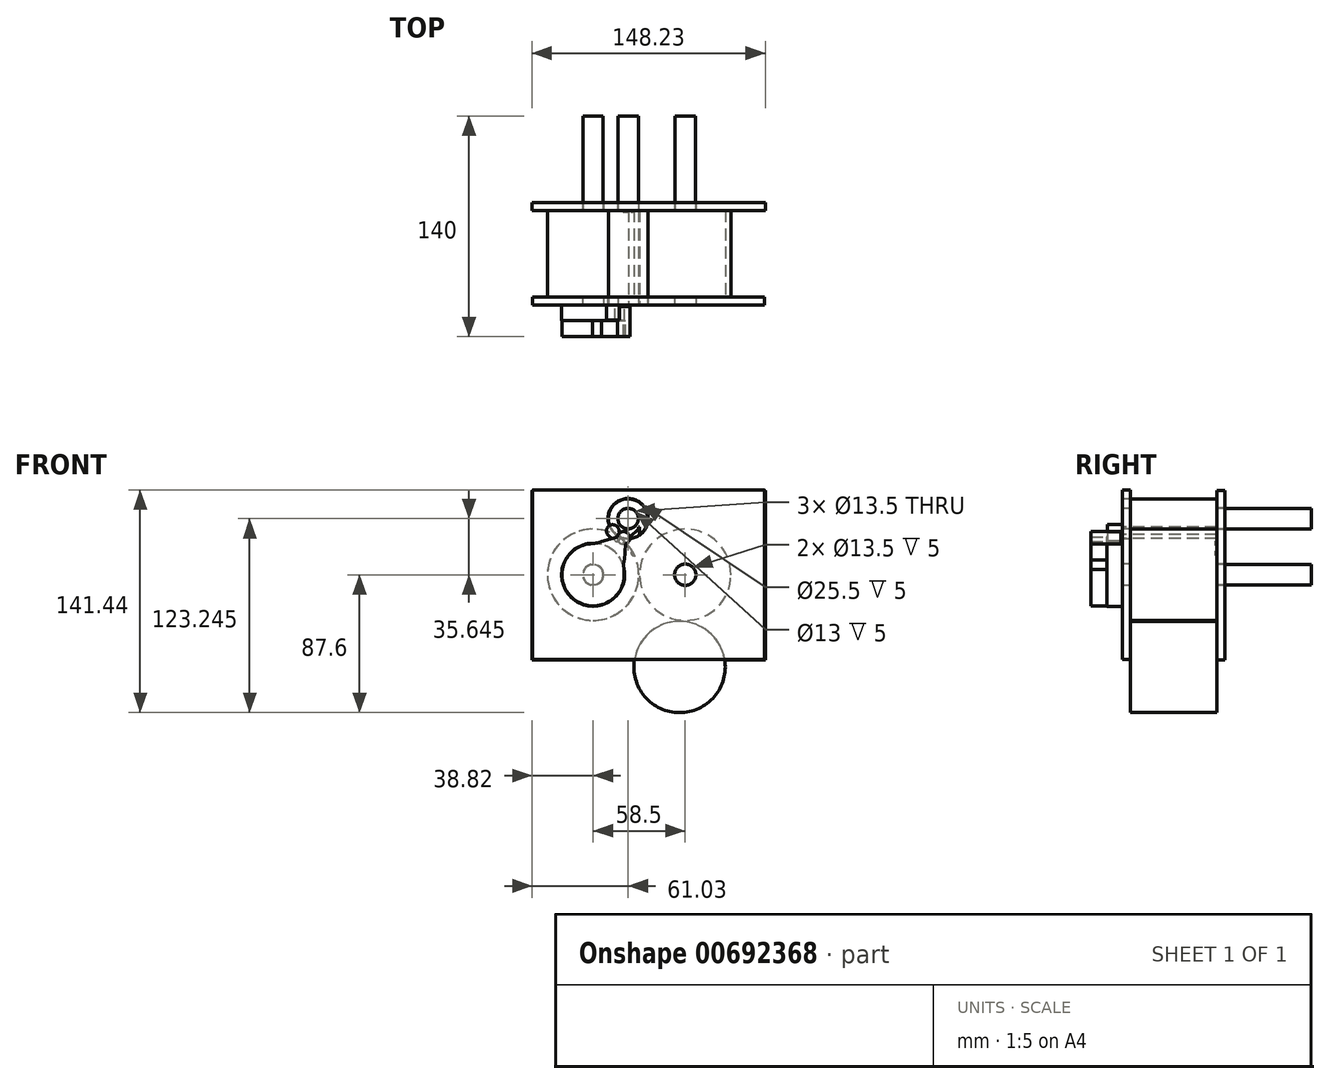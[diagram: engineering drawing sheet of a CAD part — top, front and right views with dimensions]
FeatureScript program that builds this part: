
annotation { "Feature Type Name" : "Feature", "Feature Type Description" : "" }
export const myFeature = defineFeature(function(context is Context, id is Id, definition is map)
    precondition{}
    {
        {
            var Q0;
            Q0=qCreatedBy(makeId("Front.planeOp"),FACE);
            var sketch = newSketch(context, id + "F0", { "sketchPlane" : qUnion([Q0])});
            skArc(sketch, "E0", {"start": v(-42.9, 24.45) * mm, "mid": v(-74.98, -23.86) * mm, "end": v(-41.15, 23.24) * mm});
            skArc(sketch, "E1", {"start": v(-29, 0) * mm, "mid": v(28.64, -4.55) * mm, "end": v(-27.57, 8.99) * mm});
            skCircle(sketch, "E2", {"center": v(-18.44, -37.73) * mm, "radius": 12.5 * mm});
            skCircle(sketch, "E3", {"center": v(-3.57, -58.6) * mm, "radius": 29 * mm});
            skPoint(sketch, "E4.end.orphan", {"position": v(-29.02, 40.63) * mm});
            skPoint(sketch, "E5.orphan", {"position": v(-29.02, 38.55) * mm});
            skPoint(sketch, "E6.orphan", {"position": v(-29.02, 31.65) * mm});
            skPoint(sketch, "E7.start.orphan", {"position": v(-40.21, 34.8) * mm});
            skPoint(sketch, "E8.start.orphan", {"position": v(-29.02, 34.8) * mm});
            skPoint(sketch, "E9.start.orphan", {"position": v(-29.02, 28.5) * mm});
            skLineSegment(sketch, "E10", {"start": v(-28.97, 1.35) * mm, "end": v(-29, 1.35) * mm});
            skPoint(sketch, "E11.orphan", {"position": v(-27.57, 13.81) * mm});
            skPoint(sketch, "E12.endSnap0", {"position": v(-28.5, 2.55) * mm});
            skLineSegment(sketch, "E13", {"start": v(6.21, -31.3) * mm, "end": v(1.47, -32.78) * mm});
            skLineSegment(sketch, "E14", {"start": v(-29.02, 28.5) * mm, "end": v(-29.02, 29) * mm});
            skPoint(sketch, "E15.start.orphan", {"position": v(-48.55, 37.66) * mm});
            skPoint(sketch, "E16.orphan", {"position": v(-57.21, 3.62) * mm});
            skPoint(sketch, "E17.orphan", {"position": v(-63.6, -15.91) * mm});
            skPoint(sketch, "E18.orphan", {"position": v(-48.66, 40.63) * mm});
            skPoint(sketch, "E19.orphan", {"position": v(15.22, 40.63) * mm});
            skPoint(sketch, "E20.start.orphan", {"position": v(13.58, 48.81) * mm});
            skPoint(sketch, "E21.center.orphan", {"position": v(14.4, 44.72) * mm});
            skArc(sketch, "E22.trimOffspring", {"start": v(-63.62, -9.18) * mm, "mid": v(-63.62, -9.18) * mm, "end": v(-63.6, -9.18) * mm});
            skPoint(sketch, "E23.start.orphan", {"position": v(-46.66, 44.1) * mm});
            skPoint(sketch, "E24.center.orphan", {"position": v(-44.88, 44.1) * mm});
            skPoint(sketch, "E25.trimOffspring.start.orphan", {"position": v(-29.02, 29) * mm});
            skPoint(sketch, "E26.orphan", {"position": v(-50.88, 37.66) * mm});
            skPoint(sketch, "E27.end.orphan", {"position": v(-31.73, 29) * mm});
            skPoint(sketch, "E28.orphan", {"position": v(-45.99, 26.74) * mm});
            skPoint(sketch, "E29.center.orphan", {"position": v(-55.66, 3.62) * mm});
            skPoint(sketch, "E30.trimOffspring.end.orphan", {"position": v(-54.97, 9.17) * mm});
            skPoint(sketch, "E31.center.orphan", {"position": v(-53.8, 9.17) * mm});
            skPoint(sketch, "E12.end.orphan", {"position": v(-28.5, 3.54) * mm});
            skPoint(sketch, "E32.start.orphan", {"position": v(-29, 3.74) * mm});
            skPoint(sketch, "E33.center.orphan", {"position": v(-63.6, -1.9) * mm});
            skPoint(sketch, "E34.end.orphan", {"position": v(6.08, 26.74) * mm});
            skLineSegment(sketch, "E35.trimOffspring", {"start": v(-28.98, -31) * mm, "end": v(-28.97, -38.02) * mm});
            skPoint(sketch, "E36.orphan", {"position": v(-28, 1.35) * mm});
            skArc(sketch, "E37", {"start": v(-27.57, 8.99) * mm, "mid": v(-28.64, 4.55) * mm, "end": v(-29, 0) * mm});
            skLineSegment(sketch, "E38", {"start": v(-29, 0) * mm, "end": v(-29.5, 0) * mm});
            skLineSegment(sketch, "E39", {"start": v(-29.25, 0) * mm, "end": v(-29.25, 5) * mm});
            skLineSegment(sketch, "E40", {"start": v(-29.75, 30.46) * mm, "end": v(-29.75, 29.04) * mm});
            skLineSegment(sketch, "E41", {"start": v(-29.05, 25.46) * mm, "end": v(-29.05, 30.46) * mm});
            skLineSegment(sketch, "E42", {"start": v(-29.05, 30.46) * mm, "end": v(-29.75, 30.46) * mm});
            skLineSegment(sketch, "E43", {"start": v(-29.75, 29.04) * mm, "end": v(-36, 23.15) * mm});
            skArc(sketch, "E44.trimOffspring", {"start": v(-29.05, 28.75) * mm, "mid": v(-29.04, 28.76) * mm, "end": v(-29.02, 28.78) * mm});
            skPoint(sketch, "E45.start.orphan", {"position": v(-43.7, 32.57) * mm});
            skPoint(sketch, "E46.orphan", {"position": v(-50.05, 29.86) * mm});
            skPoint(sketch, "E47.center.orphan", {"position": v(-47.7, 29) * mm});
            skLineSegment(sketch, "E48", {"start": v(-36.3, 35.64) * mm, "end": v(-58.26, 0.38) * mm, "construction": true});
            skArc(sketch, "E49", {"start": v(-33, 13.81) * mm, "mid": v(-36.56, 18.98) * mm, "end": v(-41.16, 23.25) * mm});
            skLineSegment(sketch, "E50", {"start": v(-33, 13.81) * mm, "end": v(-54, 2.44) * mm, "construction": true});
            skLineSegment(sketch, "E51", {"start": v(-29.05, 25.46) * mm, "end": v(-36.3, 35.64) * mm, "construction": true});
            skPoint(sketch, "E52.start.orphan", {"position": v(-58.26, -4.58) * mm});
            skLineSegment(sketch, "E53.trimOffspring", {"start": v(-58.26, 0.22) * mm, "end": v(-58.26, 0.38) * mm});
            skLineSegment(sketch, "E54", {"start": v(-54, 2.44) * mm, "end": v(-58.5, 0) * mm, "construction": true});
            skLineSegment(sketch, "E55", {"start": v(-36.3, 35.64) * mm, "end": v(-48.55, 37.66) * mm, "construction": true});
            skCircle(sketch, "E56", {"center": v(-58.5, 0) * mm, "radius": 12.5 * mm, "construction": true});
            skLineSegment(sketch, "E57", {"start": v(-36.35, 35.61) * mm, "end": v(-36.35, 35.55) * mm});
            skPoint(sketch, "E58.orphan", {"position": v(-36.35, 0) * mm});
            skLineSegment(sketch, "E59.trimOffspring", {"start": v(-36.35, 18.73) * mm, "end": v(-36.35, 18.72) * mm});
            skArc(sketch, "E60", {"start": v(-41.15, 23.24) * mm, "mid": v(-41.16, 23.25) * mm, "end": v(-41.16, 23.25) * mm});
            skLineSegment(sketch, "E61", {"start": v(-65.94, 8.19) * mm, "end": v(-67.94, 8.19) * mm, "construction": true});
            skPoint(sketch, "E62.orphan", {"position": v(-46.66, 42.63) * mm});
            skPoint(sketch, "E63.orphan", {"position": v(-48.66, 37.46) * mm});
            skPoint(sketch, "E64.orphan", {"position": v(-42.9, 24.45) * mm});
            skArc(sketch, "E65.trimOffspring", {"start": v(-41.97, 24.5) * mm, "mid": v(-41.97, 24.5) * mm, "end": v(-41.97, 24.51) * mm});
            skPoint(sketch, "E66.trimOffspring.start.orphan", {"position": v(-42.9, 25.04) * mm});
            skArc(sketch, "E67", {"start": v(-29.05, 25.46) * mm, "mid": v(-40.23, 47.5) * mm, "end": v(-36, 23.15) * mm});
            skArc(sketch, "E68", {"start": v(-41.15, 23.24) * mm, "mid": v(-42.02, 23.86) * mm, "end": v(-42.9, 24.45) * mm});
            skSolve(sketch);
        }
        {
            var Q0;
            {var subQ3=sQuery(id+"F0.wireOp",EDGE,"r47COwFi-Acjm-nnQF-cSEh-PlwsCDjusnOr");Q0=makeQuery(id+"F0.imprint","IMPRINT",FACE,{"disambiguationData":[TD([[makeQuery(id+"F0.imprint","IMPRINT",EDGE,{"derivedFrom":subQ3}),1.0]])]});}
            var Q1;
            {var subQ0=sQuery(id+"F0.wireOp",EDGE,"08DHOxzo-aiXv-3IRN-8knT-PrcTZCykC5HR");var subQ1=sQuery(id+"F0.wireOp",EDGE,"r47COwFi-Acjm-nnQF-cSEh-PlwsCDjusnOr");var subQ2=makeQuery(id+"F0.imprint","INTERSECT",VERTEX,{"derivedFrom":[subQ1,subQ0]});Q1=makeQuery(id+"F0.imprint","IMPRINT",FACE,{"disambiguationData":[TD([[makeQuery(id+"F0.imprint","IMPRINT",EDGE,{"disambiguationData":[TD([[subQ2,-1.0]])],"derivedFrom":subQ1}),1.0]])]});}
            var Q2;
            {var subQ0=sQuery(id+"F0.wireOp",EDGE,"Znz77gqg-z4Dj-Oz2s-iTKO-5QqTS4egn9Re");Q2=makeQuery(id+"F0.imprint","IMPRINT",FACE,{"disambiguationData":[TD([[makeQuery(id+"F0.imprint","IMPRINT",EDGE,{"derivedFrom":subQ0}),1.0]])]});}
            var Q3;
            Q3=makeQuery(id+"F0.imprint","IMPRINT",FACE,{"disambiguationData":[TD([[makeQuery(id+"F0.imprint","IMPRINT",EDGE,{"derivedFrom":sQuery(id+"F0.wireOp",EDGE,"VNmRkOMM-aoWN-BuzY-nrXP-Wf441W98SkUD")}),-1.0]])]});
            var Q4;
            {var subQ0=sQuery(id+"F0.wireOp",EDGE,"E49");var subQ1=sQuery(id+"F0.wireOp",EDGE,"E0");var subQ2=makeQuery(id+"F0.imprint","INTERSECT",VERTEX,{"disambiguationData":[OD(0.0)],"derivedFrom":[subQ1,subQ0]});Q4=makeQuery(id+"F0.imprint","IMPRINT",FACE,{"disambiguationData":[TD([[makeQuery(id+"F0.imprint","IMPRINT",EDGE,{"disambiguationData":[TD([[subQ2,1.0]])],"derivedFrom":subQ1}),1.0]])]});}
            var Q5;
            {var subQ0=sQuery(id+"F0.wireOp",EDGE,"E37");var subQ5=makeQuery(id+"F0.imprint","IMPRINT",VERTEX,{"derivedFrom":subQ0});Q5=makeQuery(id+"F0.imprint","IMPRINT",FACE,{"disambiguationData":[TD([[makeQuery(id+"F0.imprint","IMPRINT",EDGE,{"disambiguationData":[TD([[subQ5,1.0]])],"derivedFrom":subQ0}),1.0]])]});}
            var Q6;
            {var subQ0=sQuery(id+"F0.wireOp",EDGE,"E37");var subQ1=sQuery(id+"F0.wireOp",EDGE,"E1");var subQ2=makeQuery(id+"F0.imprint","INTERSECT",VERTEX,{"derivedFrom":[subQ1,subQ0]});Q6=makeQuery(id+"F0.imprint","IMPRINT",FACE,{"disambiguationData":[TD([[makeQuery(id+"F0.imprint","IMPRINT",EDGE,{"disambiguationData":[TD([[subQ2,1.0]])],"derivedFrom":subQ1}),1.0]])]});}
            extrude(context, id + "F1", {"entities" : qUnion([Q0, Q1, Q2, Q3, Q4, Q5, Q6]), "oppositeDirection" : true, "depth" : 55 * mm, "offsetDistance" : 25 * mm});
        }
        {
            var Q0;
            {var subQ5=sQuery(id+"F0.wireOp",EDGE,"Anp6vYiv-dGGn-RwVh-uZnu-5z8Qn6SWbec1");Q0=makeQuery(id+"F0.imprint","IMPRINT",FACE,{"disambiguationData":[TD([[makeQuery(id+"F0.imprint","IMPRINT",EDGE,{"derivedFrom":subQ5}),-1.0]])]});}
            var Q1;
            {var subQ0=sQuery(id+"F0.wireOp",EDGE,"VNmRkOMM-aoWN-BuzY-nrXP-Wf441W98SkUD");var subQ7=sQuery(id+"F0.wireOp",EDGE,"73RBFj6Y-QzV3-FRgO-Pfg9-x2SBzkXSbbXk");var subQ8=makeQuery(id+"F0.imprint","INTERSECT",VERTEX,{"disambiguationData":[OD(0.0)],"derivedFrom":[subQ7,subQ0]});Q1=makeQuery(id+"F0.imprint","IMPRINT",FACE,{"disambiguationData":[TD([[makeQuery(id+"F0.imprint","IMPRINT",EDGE,{"disambiguationData":[TD([[subQ8,1.0]])],"derivedFrom":subQ7}),-1.0]])]});}
            var Q2;
            {var subQ0=sQuery(id+"F0.wireOp",EDGE,"VNmRkOMM-aoWN-BuzY-nrXP-Wf441W98SkUD");var subQ1=sQuery(id+"F0.wireOp",EDGE,"Yn2ByNjK-y3Ht-DEth-yDHH-7eJyFr0YZt5b");var subQ2=makeQuery(id+"F0.imprint","INTERSECT",VERTEX,{"disambiguationData":[OD(0.0)],"derivedFrom":[subQ1,subQ0]});Q2=makeQuery(id+"F0.imprint","IMPRINT",FACE,{"disambiguationData":[TD([[makeQuery(id+"F0.imprint","IMPRINT",EDGE,{"disambiguationData":[TD([[subQ2,-1.0]])],"derivedFrom":subQ1}),1.0]])]});}
            var Q3;
            {var subQ0=sQuery(id+"F0.wireOp",EDGE,"VNmRkOMM-aoWN-BuzY-nrXP-Wf441W98SkUD");var subQ1=sQuery(id+"F0.wireOp",EDGE,"XBTpbCpp-pdxf-peGh-XHIA-OvwIBgZWktji");var subQ2=makeQuery(id+"F0.imprint","INTERSECT",VERTEX,{"disambiguationData":[OD(0.0)],"derivedFrom":[subQ1,subQ0]});Q3=makeQuery(id+"F0.imprint","IMPRINT",FACE,{"disambiguationData":[TD([[makeQuery(id+"F0.imprint","IMPRINT",EDGE,{"disambiguationData":[TD([[subQ2,-1.0]])],"derivedFrom":subQ1}),-1.0]])]});}
            var Q4;
            {var subQ1=sQuery(id+"F0.wireOp",EDGE,"Anp6vYiv-dGGn-RwVh-uZnu-5z8Qn6SWbec1");Q4=makeQuery(id+"F0.imprint","IMPRINT",FACE,{"disambiguationData":[TD([[makeQuery(id+"F0.imprint","IMPRINT",EDGE,{"derivedFrom":subQ1}),1.0]])]});}
            var Q5;
            Q5=makeQuery(id+"F0.imprint","IMPRINT",FACE,{"disambiguationData":[TD([[makeQuery(id+"F0.imprint","IMPRINT",EDGE,{"derivedFrom":sQuery(id+"F0.wireOp",EDGE,"E40")}),-1.0]])]});
            var Q6;
            {var subQ4=sQuery(id+"F0.wireOp",EDGE,"XMn3EKPV-FLZi-efLg-EMuB-rqxzckBPXCjp");Q6=makeQuery(id+"F0.imprint","IMPRINT",FACE,{"disambiguationData":[TD([[makeQuery(id+"F0.imprint","IMPRINT",EDGE,{"derivedFrom":subQ4}),-1.0]])]});}
            var Q7;
            {var subQ0=sQuery(id+"F0.wireOp",EDGE,"E3");var subQ4=makeQuery(id+"F0.imprint","IMPRINT",VERTEX,{"derivedFrom":subQ0});Q7=makeQuery(id+"F0.imprint","IMPRINT",FACE,{"disambiguationData":[TD([[makeQuery(id+"F0.imprint","IMPRINT",EDGE,{"disambiguationData":[TD([[subQ4,-1.0]])],"derivedFrom":subQ0}),1.0]])]});}
            var Q8;
            {var subQ0=sQuery(id+"F0.wireOp",EDGE,"E3");var subQ1=sQuery(id+"F0.wireOp",EDGE,"E2");var subQ2=makeQuery(id+"F0.imprint","INTERSECT",VERTEX,{"disambiguationData":[OD(0.0)],"derivedFrom":[subQ1,subQ0]});Q8=makeQuery(id+"F0.imprint","IMPRINT",FACE,{"disambiguationData":[TD([[makeQuery(id+"F0.imprint","IMPRINT",EDGE,{"disambiguationData":[TD([[subQ2,1.0]])],"derivedFrom":subQ1}),1.0]])]});}
            var Q9;
            {var subQ0=sQuery(id+"F0.wireOp",EDGE,"VNmRkOMM-aoWN-BuzY-nrXP-Wf441W98SkUD");var subQ1=sQuery(id+"F0.wireOp",EDGE,"73RBFj6Y-QzV3-FRgO-Pfg9-x2SBzkXSbbXk");var subQ2=makeQuery(id+"F0.imprint","INTERSECT",VERTEX,{"disambiguationData":[OD(0.0)],"derivedFrom":[subQ1,subQ0]});Q9=makeQuery(id+"F0.imprint","IMPRINT",FACE,{"disambiguationData":[TD([[makeQuery(id+"F0.imprint","IMPRINT",EDGE,{"disambiguationData":[TD([[subQ2,1.0]])],"derivedFrom":subQ1}),1.0]])]});}
            var Q10;
            {var subQ0=sQuery(id+"F0.wireOp",EDGE,"VNmRkOMM-aoWN-BuzY-nrXP-Wf441W98SkUD");var subQ1=sQuery(id+"F0.wireOp",EDGE,"73RBFj6Y-QzV3-FRgO-Pfg9-x2SBzkXSbbXk");var subQ2=makeQuery(id+"F0.imprint","INTERSECT",VERTEX,{"disambiguationData":[OD(0.0)],"derivedFrom":[subQ1,subQ0]});Q10=makeQuery(id+"F0.imprint","IMPRINT",FACE,{"disambiguationData":[TD([[makeQuery(id+"F0.imprint","IMPRINT",EDGE,{"disambiguationData":[TD([[subQ2,-1.0]])],"derivedFrom":subQ1}),1.0]])]});}
            var Q11;
            Q11=makeQuery(id+"F0.imprint","IMPRINT",FACE,{"disambiguationData":[TD([[makeQuery(id+"F0.imprint","IMPRINT",EDGE,{"derivedFrom":sQuery(id+"F0.wireOp",EDGE,"XMn3EKPV-FLZi-efLg-EMuB-rqxzckBPXCjp")}),1.0]])]});
            var Q12;
            {var subQ0=sQuery(id+"F0.wireOp",EDGE,"VNmRkOMM-aoWN-BuzY-nrXP-Wf441W98SkUD");var subQ1=sQuery(id+"F0.wireOp",EDGE,"Yn2ByNjK-y3Ht-DEth-yDHH-7eJyFr0YZt5b");var subQ2=makeQuery(id+"F0.imprint","INTERSECT",VERTEX,{"derivedFrom":[subQ1,subQ0]});Q12=makeQuery(id+"F0.imprint","IMPRINT",FACE,{"disambiguationData":[TD([[makeQuery(id+"F0.imprint","IMPRINT",EDGE,{"disambiguationData":[TD([[subQ2,-1.0]])],"derivedFrom":subQ1}),-1.0]])]});}
            var Q13;
            Q13=makeQuery(id+"F0.imprint","IMPRINT",FACE,{"disambiguationData":[TD([[makeQuery(id+"F0.imprint","IMPRINT",EDGE,{"derivedFrom":sQuery(id+"F0.wireOp",EDGE,"73RBFj6Y-QzV3-FRgO-Pfg9-x2SBzkXSbbXk")}),1.0]])]});
            var Q14;
            {var subQ0=sQuery(id+"F0.wireOp",EDGE,"08DHOxzo-aiXv-3IRN-8knT-PrcTZCykC5HR");var subQ1=sQuery(id+"F0.wireOp",EDGE,"r47COwFi-Acjm-nnQF-cSEh-PlwsCDjusnOr");var subQ2=makeQuery(id+"F0.imprint","INTERSECT",VERTEX,{"derivedFrom":[subQ1,subQ0]});Q14=makeQuery(id+"F0.imprint","IMPRINT",FACE,{"disambiguationData":[TD([[makeQuery(id+"F0.imprint","IMPRINT",EDGE,{"disambiguationData":[TD([[subQ2,-1.0]])],"derivedFrom":subQ1}),1.0]])]});}
            var Q15;
            {var subQ0=sQuery(id+"F0.wireOp",EDGE,"Znz77gqg-z4Dj-Oz2s-iTKO-5QqTS4egn9Re");Q15=makeQuery(id+"F0.imprint","IMPRINT",FACE,{"disambiguationData":[TD([[makeQuery(id+"F0.imprint","IMPRINT",EDGE,{"derivedFrom":subQ0}),1.0]])]});}
            extrude(context, id + "F2", {"entities" : qUnion([Q0, Q1, Q2, Q3, Q4, Q5, Q6, Q7, Q8, Q9, Q10, Q11, Q12, Q13, Q14, Q15]), "operationType" : NewBodyOperationType.ADD, "oppositeDirection" : true, "depth" : 55 * mm, "offsetDistance" : 25 * mm});
        }
        {
            var Q0;
            Q0=makeQuery(id+"F2.opExtrude","CAP_FACE",FACE,{"disambiguationData":[OSD([sQuery(id+"F0.wireOp",EDGE,"E40"),sQuery(id+"F0.wireOp",EDGE,"E41"),sQuery(id+"F0.wireOp",EDGE,"E42"),sQuery(id+"F0.wireOp",EDGE,"E43"),sQuery(id+"F0.wireOp",EDGE,"E67")])],"isStart":true});
            extrude(context, id + "F3", {"entities" : qUnion([Q0]), "operationType" : NewBodyOperationType.ADD, "depth" : 5 * mm, "offsetDistance" : 25 * mm});
        }
        {
            var Q0;
            Q0=makeQuery(id+"F1.opExtrude","CAP_FACE",FACE,{"disambiguationData":[OSD([sQuery(id+"F0.wireOp",EDGE,"E0"),sQuery(id+"F0.wireOp",EDGE,"E68")])],"isStart":true});
            var sketch = newSketch(context, id + "F4", { "sketchPlane" : qUnion([Q0])});
            skCircle(sketch, "E69", {"center": v(-36.3, 35.64) * mm, "radius": 12.75 * mm});
            skLineSegment(sketch, "E70.bottom", {"start": v(-96.84, 53.84) * mm, "end": v(50.2, 53.84) * mm});
            skLineSegment(sketch, "E70.top", {"start": v(-96.84, -53.8) * mm, "end": v(50.2, -53.8) * mm});
            skLineSegment(sketch, "E70.left", {"start": v(-96.84, 53.84) * mm, "end": v(-96.84, -53.8) * mm});
            skLineSegment(sketch, "E70.right", {"start": v(50.2, 53.84) * mm, "end": v(50.2, -53.8) * mm});
            skSolve(sketch);
        }
        {
            var Q0;
            Q0 = qSketchRegion(id + "F4", true);
            extrude(context, id + "F5", {"entities" : qUnion([Q0]), "depth" : 5 * mm, "offsetDistance" : 25 * mm});
        }
        {
            var Q0;
            Q0=makeQuery(id+"F1.opExtrude","CAP_FACE",FACE,{"disambiguationData":[OSD([sQuery(id+"F0.wireOp",EDGE,"E1"),sQuery(id+"F0.wireOp",EDGE,"E37")])],"isStart":false});
            var sketch = newSketch(context, id + "F6", { "sketchPlane" : qUnion([Q0])});
            skCircle(sketch, "E71", {"center": v(0, 0) * mm, "radius": 6.5 * mm});
            skCircle(sketch, "E72", {"center": v(58.5, 0) * mm, "radius": 6.37 * mm});
            skCircle(sketch, "E73", {"center": v(36.3, 35.64) * mm, "radius": 6.5 * mm});
            skSolve(sketch);
        }
        {
            var Q0;
            Q0 = qSketchRegion(id + "F6", true);
            extrude(context, id + "F7", {"entities" : qUnion([Q0]), "operationType" : NewBodyOperationType.ADD, "endBound" : BoundingType.SYMMETRIC, "depth" : 120 * mm, "offsetDistance" : 25 * mm});
        }
        {
            var Q0;
            Q0=makeQuery(id+"F5.opExtrude","CAP_FACE",FACE,{"disambiguationData":[OSD([sQuery(id+"F4.wireOp",EDGE,"E69"),sQuery(id+"F4.wireOp",EDGE,"E70.bottom"),sQuery(id+"F4.wireOp",EDGE,"E70.top"),sQuery(id+"F4.wireOp",EDGE,"E70.left"),sQuery(id+"F4.wireOp",EDGE,"E70.right")])],"isStart":false});
            var sketch = newSketch(context, id + "F8", { "sketchPlane" : qUnion([Q0])});
            skCircle(sketch, "E74", {"center": v(0, 0) * mm, "radius": 6.75 * mm});
            skCircle(sketch, "E75", {"center": v(-58.5, 0) * mm, "radius": 6.75 * mm});
            skCircle(sketch, "E76", {"center": v(-36.3, 35.64) * mm, "radius": 6.5 * mm});
            skSolve(sketch);
        }
        {
            var Q0;
            Q0 = qSketchRegion(id + "F8", true);
            extrude(context, id + "F9", {"entities" : qUnion([Q0]), "operationType" : NewBodyOperationType.REMOVE, "oppositeDirection" : true, "depth" : 5 * mm, "offsetDistance" : 25 * mm});
        }
        {
            var Q0;
            Q0=makeQuery(id+"F1.opExtrude","CAP_FACE",FACE,{"disambiguationData":[OSD([sQuery(id+"F0.wireOp",EDGE,"E1"),sQuery(id+"F0.wireOp",EDGE,"E37")])],"isStart":false});
            var sketch = newSketch(context, id + "F10", { "sketchPlane" : qUnion([Q0])});
            skLineSegment(sketch, "E77.bottom", {"start": v(-50.9, -54.05) * mm, "end": v(97.32, -54.05) * mm});
            skLineSegment(sketch, "E77.top", {"start": v(-50.9, 53.59) * mm, "end": v(97.32, 53.59) * mm});
            skLineSegment(sketch, "E77.left", {"start": v(-50.9, -54.05) * mm, "end": v(-50.9, 53.59) * mm});
            skLineSegment(sketch, "E77.right", {"start": v(97.32, -54.05) * mm, "end": v(97.32, 53.59) * mm});
            skCircle(sketch, "E78", {"center": v(58.5, 0) * mm, "radius": 6.75 * mm});
            skCircle(sketch, "E79", {"center": v(0, 0) * mm, "radius": 6.75 * mm});
            skCircle(sketch, "E80", {"center": v(36.3, 35.64) * mm, "radius": 6.75 * mm});
            skSolve(sketch);
        }
        {
            var Q0;
            Q0=makeQuery(id+"F10.imprint","IMPRINT",FACE,{"disambiguationData":[TD([[makeQuery(id+"F10.imprint","IMPRINT",EDGE,{"derivedFrom":sQuery(id+"F10.wireOp",EDGE,"E77.bottom")}),1.0]])]});
            var Q1;
            Q1=makeQuery(id+"F10.imprint","IMPRINT",FACE,{"disambiguationData":[TD([[makeQuery(id+"F10.imprint","IMPRINT",EDGE,{"derivedFrom":sQuery(id+"F10.wireOp",EDGE,"E79")}),-1.0]])]});
            extrude(context, id + "F11", {"entities" : qUnion([Q0, Q1]), "depth" : 5 * mm, "offsetDistance" : 25 * mm});
        }
        {
            var Q0;
            Q0=makeQuery(id+"F5.opExtrude","CAP_FACE",FACE,{"disambiguationData":[OSD([sQuery(id+"F4.wireOp",EDGE,"E69"),sQuery(id+"F4.wireOp",EDGE,"E70.bottom"),sQuery(id+"F4.wireOp",EDGE,"E70.top"),sQuery(id+"F4.wireOp",EDGE,"E70.left"),sQuery(id+"F4.wireOp",EDGE,"E70.right")])],"isStart":false});
            var sketch = newSketch(context, id + "F12", { "sketchPlane" : qUnion([Q0])});
            skCircle(sketch, "E81", {"center": v(-58.5, 0) * mm, "radius": 20 * mm});
            skSolve(sketch);
        }
        {
            var Q0;
            Q0 = qSketchRegion(id + "F12", true);
            extrude(context, id + "F13", {"entities" : qUnion([Q0]), "operationType" : NewBodyOperationType.ADD, "depth" : 10 * mm, "offsetDistance" : 25 * mm});
        }
        {
            var Q0;
            Q0=makeQuery(id+"F3.opExtrude","CAP_FACE",FACE,{"disambiguationData":[OSD([sQuery(id+"F0.wireOp",EDGE,"E40"),sQuery(id+"F0.wireOp",EDGE,"E41"),sQuery(id+"F0.wireOp",EDGE,"E42"),sQuery(id+"F0.wireOp",EDGE,"E43"),sQuery(id+"F0.wireOp",EDGE,"E67")])],"isStart":false});
            var sketch = newSketch(context, id + "F14", { "sketchPlane" : qUnion([Q0])});
            skArc(sketch, "E82", {"start": v(-42.04, 28.18) * mm, "mid": v(-47.06, 31.66) * mm, "end": v(-49.66, 26.13) * mm});
            skArc(sketch, "E83", {"start": v(-44.66, 21.69) * mm, "mid": v(-42.56, 21.4) * mm, "end": v(-41.54, 23.25) * mm});
            skLineSegment(sketch, "E84", {"start": v(-42.04, 28.22) * mm, "end": v(-41.54, 23.25) * mm});
            skLineSegment(sketch, "E85", {"start": v(-44.66, 21.69) * mm, "end": v(-48.47, 24.63) * mm});
            skArc(sketch, "E86.trimOffspring", {"start": v(-42.04, 28.18) * mm, "mid": v(-42.04, 28.2) * mm, "end": v(-42.04, 28.22) * mm});
            skArc(sketch, "E87.trimOffspring", {"start": v(-49.66, 26.13) * mm, "mid": v(-49.15, 25.3) * mm, "end": v(-48.47, 24.63) * mm});
            skSolve(sketch);
        }
        {
            var Q0;
            Q0 = qSketchRegion(id + "F14", true);
            extrude(context, id + "F15", {"entities" : qUnion([Q0]), "operationType" : NewBodyOperationType.ADD, "depth" : 9.6 * mm, "offsetDistance" : 25 * mm});
        }
        {
            var Q0;
            Q0=makeQuery(id+"F1.opExtrude","CAP_FACE",FACE,{"disambiguationData":[OSD([sQuery(id+"F0.wireOp",EDGE,"E0"),sQuery(id+"F0.wireOp",EDGE,"E68")])],"isStart":false});
            var sketch = newSketch(context, id + "F16", { "sketchPlane" : qUnion([Q0])});
            skCircle(sketch, "E88", {"center": v(32.97, 13.76) * mm, "radius": 1.47 * mm});
            skCircle(sketch, "E89", {"center": v(37.79, 20.3) * mm, "radius": 1.58 * mm});
            skSolve(sketch);
        }
        {
            var Q0;
            Q0 = qSketchRegion(id + "F16", true);
            extrude(context, id + "F17", {"entities" : qUnion([Q0]), "operationType" : NewBodyOperationType.REMOVE, "oppositeDirection" : true, "depth" : 1 * mm, "offsetDistance" : 25 * mm});
        }
        {
            var Q0;
            Q0=makeQuery(id+"F13.opExtrude","CAP_FACE",FACE,{"disambiguationData":[OSD([sQuery(id+"F12.wireOp",EDGE,"E81")])],"isStart":false});
            var sketch = newSketch(context, id + "F18", { "sketchPlane" : qUnion([Q0])});
            skArc(sketch, "E90", {"start": v(-58.87, 19.77) * mm, "mid": v(-71.09, -15.25) * mm, "end": v(-39.02, 3.38) * mm});
            skCircle(sketch, "E91", {"center": v(-39.2, 23.38) * mm, "radius": 4 * mm});
            skLineSegment(sketch, "E92", {"start": v(-58.5, 0) * mm, "end": v(-39.2, 23.38) * mm, "construction": true});
            skLineSegment(sketch, "E93", {"start": v(-39.2, 23.38) * mm, "end": v(-53.38, 35.1) * mm, "construction": true});
            skArc(sketch, "E94", {"start": v(-58.87, 20) * mm, "mid": v(-55.85, 20.2) * mm, "end": v(-53.02, 21.24) * mm});
            skArc(sketch, "E95.MirrorCS", {"start": v(-38.8, 3.43) * mm, "mid": v(-39.16, 6.43) * mm, "end": v(-38.68, 9.4) * mm});
            skLineSegment(sketch, "E96", {"start": v(-58.87, 20) * mm, "end": v(-58.87, 19.77) * mm});
            skLineSegment(sketch, "E97.MirrorCS", {"start": v(-38.8, 3.43) * mm, "end": v(-39.02, 3.38) * mm});
            skPoint(sketch, "E98.orphan", {"position": v(-58.87, 17.83) * mm});
            skPoint(sketch, "E99.orphan", {"position": v(-40.92, 3.02) * mm});
            skLineSegment(sketch, "E100", {"start": v(-53.02, 21.24) * mm, "end": v(-43.14, 24.03) * mm});
            skLineSegment(sketch, "E101.MirrorCS", {"start": v(-38.68, 9.4) * mm, "end": v(-37.82, 19.63) * mm});
            skPoint(sketch, "E102.orphan", {"position": v(-48.71, 25.4) * mm});
            skPoint(sketch, "E103.orphan", {"position": v(-35.42, 14.42) * mm});
            skSolve(sketch);
        }
        {
            var Q0;
            Q0 = qSketchRegion(id + "F18", true);
            extrude(context, id + "F19", {"entities" : qUnion([Q0]), "operationType" : NewBodyOperationType.ADD, "depth" : 10 * mm, "offsetDistance" : 25 * mm});
        }
        {
            var Q0;
            Q0=makeQuery(id+"F19.opExtrude","CAP_FACE",FACE,{"disambiguationData":[OSD([sQuery(id+"F18.wireOp",EDGE,"E90"),sQuery(id+"F18.wireOp",EDGE,"E91"),sQuery(id+"F18.wireOp",EDGE,"hn3PvQAy-HSqP-sKK6-z7vQ-PZQaQBWFVtoP"),sQuery(id+"F18.wireOp",EDGE,"E94"),sQuery(id+"F18.wireOp",EDGE,"E95.MirrorCS"),sQuery(id+"F18.wireOp",EDGE,"E96"),sQuery(id+"F18.wireOp",EDGE,"E97.MirrorCS")])],"isStart":false});
            var sketch = newSketch(context, id + "F20", { "sketchPlane" : qUnion([Q0])});
            skCircle(sketch, "E104", {"center": v(-39.2, 23.38) * mm, "radius": 4 * mm});
            skSolve(sketch);
        }
        {
            var Q0;
            Q0 = qSketchRegion(id + "F20", true);
            extrude(context, id + "F21", {"entities" : qUnion([Q0]), "operationType" : NewBodyOperationType.ADD, "oppositeDirection" : true, "depth" : 19 * mm, "offsetDistance" : 25 * mm});
        }
    });
